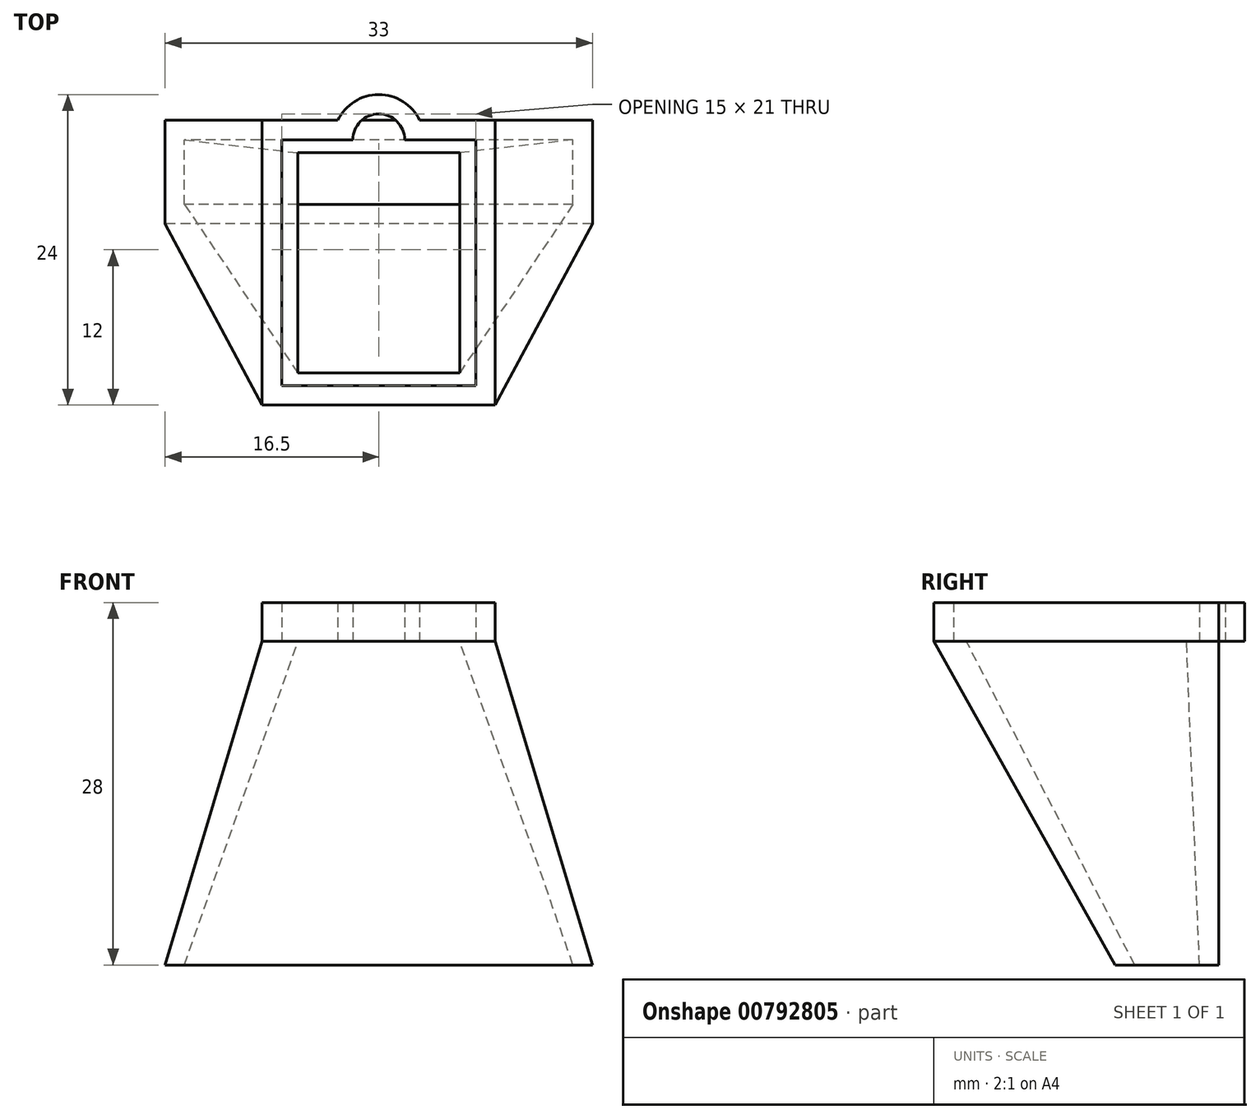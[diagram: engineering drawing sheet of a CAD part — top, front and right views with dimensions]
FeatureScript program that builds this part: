
annotation { "Feature Type Name" : "Feature", "Feature Type Description" : "" }
export const myFeature = defineFeature(function(context is Context, id is Id, definition is map)
    precondition{}
    {
        {
            var Q0;
            Q0=qCreatedBy(makeId("Top.planeOp"),FACE);
            var sketch = newSketch(context, id + "F0", { "sketchPlane" : qUnion([Q0])});
            skLineSegment(sketch, "E0.bottom", {"start": v(6.25, 8.5) * mm, "end": v(-6.25, 8.5) * mm});
            skLineSegment(sketch, "E0.top", {"start": v(6.25, -8.5) * mm, "end": v(-6.25, -8.5) * mm});
            skLineSegment(sketch, "E0.left", {"start": v(6.25, 8.5) * mm, "end": v(6.25, -8.5) * mm});
            skLineSegment(sketch, "E0.right", {"start": v(-6.25, 8.5) * mm, "end": v(-6.25, -8.5) * mm});
            skPoint(sketch, "E0.middle", {"position": v(0, 0) * mm});
            skLineSegment(sketch, "E1.bottom", {"start": v(7.5, 9.5) * mm, "end": v(-7.5, 9.5) * mm});
            skLineSegment(sketch, "E1.top", {"start": v(7.5, -9.5) * mm, "end": v(-7.5, -9.5) * mm});
            skLineSegment(sketch, "E1.left", {"start": v(7.5, 9.5) * mm, "end": v(7.5, -9.5) * mm});
            skLineSegment(sketch, "E1.right", {"start": v(-7.5, 9.5) * mm, "end": v(-7.5, -9.5) * mm});
            skSolve(sketch);
        }
        {
            var Q0;
            Q0=qCreatedBy(makeId("Top.planeOp"),FACE);
            var sketch = newSketch(context, id + "F1", { "sketchPlane" : qUnion([Q0])});
            skLineSegment(sketch, "E2.bottom", {"start": v(7.5, 9.5) * mm, "end": v(-7.5, 9.5) * mm, "construction": true});
            skLineSegment(sketch, "E2.top", {"start": v(7.5, -9.5) * mm, "end": v(-7.5, -9.5) * mm});
            skLineSegment(sketch, "E2.left", {"start": v(7.5, 9.5) * mm, "end": v(7.5, -9.5) * mm});
            skLineSegment(sketch, "E2.right", {"start": v(-7.5, 9.5) * mm, "end": v(-7.5, -9.5) * mm});
            skPoint(sketch, "E2.middle", {"position": v(0, 0) * mm});
            skLineSegment(sketch, "E3.bottom", {"start": v(9, 11) * mm, "end": v(-9, 11) * mm, "construction": true});
            skLineSegment(sketch, "E3.top", {"start": v(9, -11) * mm, "end": v(-9, -11) * mm});
            skLineSegment(sketch, "E3.left", {"start": v(9, 11) * mm, "end": v(9, -11) * mm});
            skLineSegment(sketch, "E3.right", {"start": v(-9, 11) * mm, "end": v(-9, -11) * mm});
            skArc(sketch, "E4", {"start": v(-2, 9.5) * mm, "mid": v(0, 11.5) * mm, "end": v(2, 9.5) * mm});
            skLineSegment(sketch, "E5", {"start": v(9, 11) * mm, "end": v(3.16, 11) * mm});
            skLineSegment(sketch, "E6", {"start": v(-9, 11) * mm, "end": v(-3.16, 11) * mm});
            skLineSegment(sketch, "E7", {"start": v(-2, 9.5) * mm, "end": v(-7.5, 9.5) * mm});
            skLineSegment(sketch, "E8", {"start": v(2, 9.5) * mm, "end": v(7.5, 9.5) * mm});
            skArc(sketch, "E9", {"start": v(-3.16, 11) * mm, "mid": v(0, 13) * mm, "end": v(3.16, 11) * mm});
            skSolve(sketch);
        }
        {
            var Q0;
            Q0 = qSketchRegion(id + "F1", true);
            extrude(context, id + "F2", {"entities" : qUnion([Q0]), "depth" : 3 * mm, "offsetDistance" : 25 * mm});
        }
        {
            var Q0;
            Q0=qCreatedBy(makeId("Top.planeOp"),FACE);
            var sketch = newSketch(context, id + "F3", { "sketchPlane" : qUnion([Q0])});
            skLineSegment(sketch, "E10.0", {"start": v(-9, -11) * mm, "end": v(-9, -11) * mm});
            skLineSegment(sketch, "E11.0", {"start": v(9, -11) * mm, "end": v(-9, -11) * mm});
            skLineSegment(sketch, "E12.0", {"start": v(9, -11) * mm, "end": v(9, -11) * mm});
            skLineSegment(sketch, "E13.0.0", {"start": v(-6.25, -8.5) * mm, "end": v(6.25, -8.5) * mm, "construction": true});
            skLineSegment(sketch, "E13.0.1", {"start": v(6.25, -8.5) * mm, "end": v(6.25, 8.5) * mm, "construction": true});
            skLineSegment(sketch, "E13.0.2", {"start": v(6.25, 8.5) * mm, "end": v(-6.25, 8.5) * mm, "construction": true});
            skLineSegment(sketch, "E13.0.3", {"start": v(-6.25, 8.5) * mm, "end": v(-6.25, -8.5) * mm, "construction": true});
            skLineSegment(sketch, "E14.0", {"start": v(9, 11) * mm, "end": v(9, -11) * mm});
            skLineSegment(sketch, "E15.0", {"start": v(-9, 11) * mm, "end": v(-9, -11) * mm});
            skLineSegment(sketch, "E16", {"start": v(9, 11) * mm, "end": v(-9, 11) * mm});
            skSolve(sketch);
        }
        {
            var Q0;
            Q0=qCreatedBy(makeId("Top.planeOp"),FACE);
            cPlane(context, id + "F4", {"entities" : qUnion([Q0]), "cplaneType" : CPlaneType.OFFSET, "offset" : 25 * mm, "oppositeDirection" : true, "width" : 150 * mm, "height" : 150 * mm});
        }
        {
            var Q0;
            Q0=qCreatedBy(id+"F4.planeOp",FACE);
            var sketch = newSketch(context, id + "F5", { "sketchPlane" : qUnion([Q0])});
            skPoint(sketch, "E17", {"position": v(0, 7) * mm});
            skLineSegment(sketch, "E18.bottom", {"start": v(-15, 4.5) * mm, "end": v(15, 4.5) * mm, "construction": true});
            skLineSegment(sketch, "E18.top", {"start": v(-15, 9.5) * mm, "end": v(15, 9.5) * mm, "construction": true});
            skLineSegment(sketch, "E18.left", {"start": v(-15, 4.5) * mm, "end": v(-15, 9.5) * mm, "construction": true});
            skLineSegment(sketch, "E18.right", {"start": v(15, 4.5) * mm, "end": v(15, 9.5) * mm, "construction": true});
            skLineSegment(sketch, "E19.bottom", {"start": v(16.5, 3) * mm, "end": v(-16.5, 3) * mm});
            skLineSegment(sketch, "E19.top", {"start": v(16.5, 11) * mm, "end": v(-16.5, 11) * mm});
            skLineSegment(sketch, "E19.left", {"start": v(16.5, 3) * mm, "end": v(16.5, 11) * mm});
            skLineSegment(sketch, "E19.right", {"start": v(-16.5, 3) * mm, "end": v(-16.5, 11) * mm});
            skSolve(sketch);
        }
        {
            var Q0;
            Q0=makeQuery(id+"F3.imprint","IMPRINT",FACE,{"disambiguationData":[TD([[makeQuery(id+"F3.imprint","IMPRINT",EDGE,{"derivedFrom":sQuery(id+"F3.wireOp",EDGE,"E11.0")}),-1.0]])]});
            var sketch = newSketch(context, id + "F6", { "sketchPlane" : qUnion([Q0])});
            skLineSegment(sketch, "E20.bottom", {"start": v(6.25, -8.5) * mm, "end": v(-6.25, -8.5) * mm});
            skLineSegment(sketch, "E20.top", {"start": v(6.25, 8.5) * mm, "end": v(-6.25, 8.5) * mm});
            skLineSegment(sketch, "E20.left", {"start": v(6.25, -8.5) * mm, "end": v(6.25, 8.5) * mm});
            skLineSegment(sketch, "E20.right", {"start": v(-6.25, -8.5) * mm, "end": v(-6.25, 8.5) * mm});
            skSolve(sketch);
        }
        {
            var Q0;
            Q0=makeQuery(id+"F5.imprint","IMPRINT",FACE,{"disambiguationData":[TD([[makeQuery(id+"F5.imprint","IMPRINT",EDGE,{"derivedFrom":sQuery(id+"F5.wireOp",EDGE,"E19.bottom")}),-1.0]])]});
            var sketch = newSketch(context, id + "F7", { "sketchPlane" : qUnion([Q0])});
            skLineSegment(sketch, "E21.bottom", {"start": v(15, 4.5) * mm, "end": v(-15, 4.5) * mm});
            skLineSegment(sketch, "E21.top", {"start": v(15, 9.5) * mm, "end": v(-15, 9.5) * mm});
            skLineSegment(sketch, "E21.left", {"start": v(15, 4.5) * mm, "end": v(15, 9.5) * mm});
            skLineSegment(sketch, "E21.right", {"start": v(-15, 4.5) * mm, "end": v(-15, 9.5) * mm});
            skPoint(sketch, "E21.middle", {"position": v(0, 7) * mm});
            skSolve(sketch);
        }
        {
            var Q0;
            Q0=makeQuery(id+"F3.imprint","IMPRINT",FACE,{"disambiguationData":[TD([[makeQuery(id+"F3.imprint","IMPRINT",EDGE,{"derivedFrom":sQuery(id+"F3.wireOp",EDGE,"E11.0")}),-1.0]])]});
            var Q1;
            Q1=makeQuery(id+"F5.imprint","IMPRINT",FACE,{"disambiguationData":[TD([[makeQuery(id+"F5.imprint","IMPRINT",EDGE,{"derivedFrom":sQuery(id+"F5.wireOp",EDGE,"E19.bottom")}),-1.0]])]});
            loft(context, id + "F8", {"sheetProfilesArray" : [{ "sheetProfileEntities" : qUnion([Q0]) }, { "sheetProfileEntities" : qUnion([Q1]) }]});
        }
        {
            var Q1;
            Q1 = qSketchRegion(id + "F7", true);
            var Q2;
            Q2 = qSketchRegion(id + "F6", true);
            loft(context, id + "F9", {"operationType" : NewBodyOperationType.REMOVE, "sheetProfilesArray" : [{ "sheetProfileEntities" : qUnion([Q1]) }, { "sheetProfileEntities" : qUnion([Q2]) }]});
        }
    });
